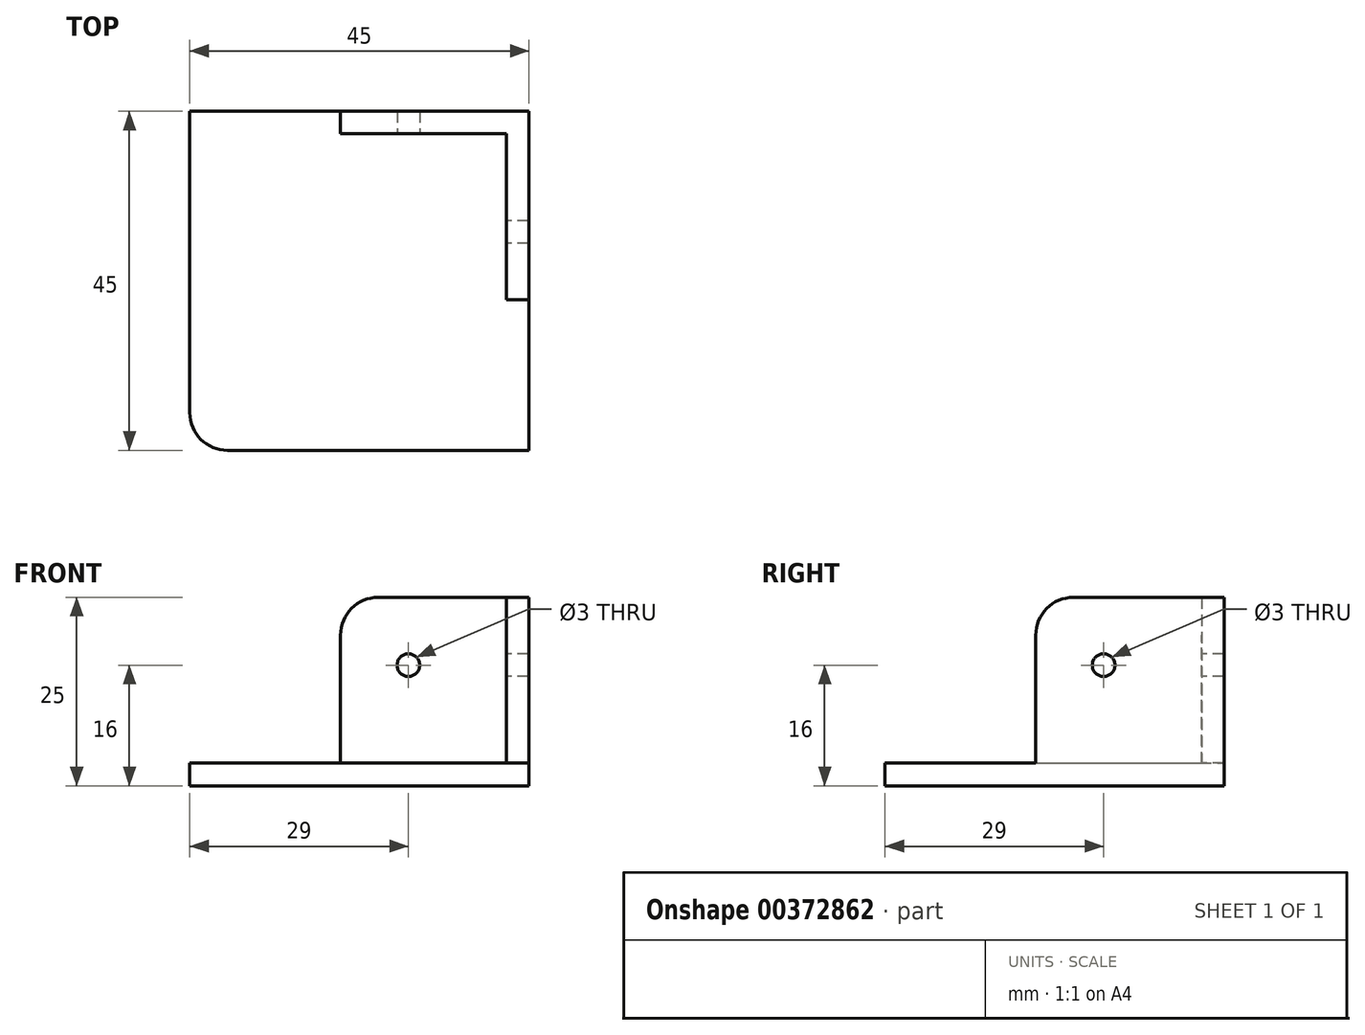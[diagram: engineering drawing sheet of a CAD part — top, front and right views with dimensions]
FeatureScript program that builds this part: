
annotation { "Feature Type Name" : "Feature", "Feature Type Description" : "" }
export const myFeature = defineFeature(function(context is Context, id is Id, definition is map)
    precondition{}
    {
        {
            var Q0;
            Q0=qCreatedBy(makeId("Top.planeOp"),FACE);
            var sketch = newSketch(context, id + "F0", { "sketchPlane" : qUnion([Q0])});
            skLineSegment(sketch, "E0.bottom", {"start": v(0, -45) * mm, "end": v(-45, -45) * mm});
            skLineSegment(sketch, "E0.top", {"start": v(0, 0) * mm, "end": v(-45, 0) * mm});
            skLineSegment(sketch, "E0.left", {"start": v(0, -45) * mm, "end": v(0, 0) * mm});
            skLineSegment(sketch, "E0.right", {"start": v(-45, -45) * mm, "end": v(-45, 0) * mm});
            skSolve(sketch);
        }
        {
            var Q0;
            Q0=qCreatedBy(makeId("Right.planeOp"),FACE);
            var sketch = newSketch(context, id + "F1", { "sketchPlane" : qUnion([Q0])});
            skLineSegment(sketch, "E1.bottom", {"start": v(-25, 0) * mm, "end": v(0, 0) * mm});
            skLineSegment(sketch, "E1.top", {"start": v(-25, 25) * mm, "end": v(0, 25) * mm});
            skLineSegment(sketch, "E1.left", {"start": v(-25, 0) * mm, "end": v(-25, 25) * mm});
            skLineSegment(sketch, "E1.right", {"start": v(0, 0) * mm, "end": v(0, 25) * mm});
            skSolve(sketch);
        }
        {
            var Q0;
            Q0=qCreatedBy(makeId("Front.planeOp"),FACE);
            var sketch = newSketch(context, id + "F2", { "sketchPlane" : qUnion([Q0])});
            skLineSegment(sketch, "E2.bottom", {"start": v(-25, 0) * mm, "end": v(0, 0) * mm});
            skLineSegment(sketch, "E2.top", {"start": v(-25, 25) * mm, "end": v(0, 25) * mm});
            skLineSegment(sketch, "E2.left", {"start": v(-25, 0) * mm, "end": v(-25, 25) * mm});
            skLineSegment(sketch, "E2.right", {"start": v(0, 0) * mm, "end": v(0, 25) * mm});
            skSolve(sketch);
        }
        {
            var Q0;
            Q0=qSketchRegion(id+"F0",true);
            extrude(context, id + "F3", {"entities" : qUnion([Q0]), "depth" : 3 * mm});
        }
        {
            var Q0;
            Q0=makeQuery(id+"F3.opExtrude","SWEPT_EDGE",EDGE,{"disambiguationData":[OSD([sQuery(id+"F0.wireOp",EDGE,"E0.bottom"),sQuery(id+"F0.wireOp",EDGE,"E0.right")])]});
            fillet(context, id + "F4", {"entities" : qUnion([Q0]), "radius" : 5 * mm, "allowEdgeOverflow" : false});
        }
        {
            var Q0;
            Q0=makeQuery(id+"F1.imprint","IMPRINT",FACE,{"disambiguationData":[TD([[makeQuery(id+"F1.imprint","IMPRINT",EDGE,{"derivedFrom":sQuery(id+"F1.wireOp",EDGE,"E1.bottom")}),1.0]])]});
            extrude(context, id + "F5", {"entities" : qUnion([Q0]), "operationType" : NewBodyOperationType.ADD, "oppositeDirection" : true, "depth" : 3 * mm});
        }
        {
            var Q0;
            Q0=makeQuery(id+"F5.opExtrude","SWEPT_EDGE",EDGE,{"disambiguationData":[OSD([sQuery(id+"F1.wireOp",EDGE,"E1.top"),sQuery(id+"F1.wireOp",EDGE,"E1.left")])]});
            fillet(context, id + "F6", {"entities" : qUnion([Q0]), "radius" : 5 * mm, "tangentPropagation" : true, "allowEdgeOverflow" : false});
        }
        {
            var Q0;
            Q0=makeQuery(id+"F2.imprint","IMPRINT",FACE,{"disambiguationData":[TD([[makeQuery(id+"F2.imprint","IMPRINT",EDGE,{"derivedFrom":sQuery(id+"F2.wireOp",EDGE,"E2.bottom")}),1.0]])]});
            extrude(context, id + "F7", {"entities" : qUnion([Q0]), "operationType" : NewBodyOperationType.ADD, "depth" : 3 * mm});
        }
        {
            var Q0;
            Q0=makeQuery(id+"F7.opExtrude","SWEPT_EDGE",EDGE,{"disambiguationData":[OSD([sQuery(id+"F2.wireOp",EDGE,"E2.top"),sQuery(id+"F2.wireOp",EDGE,"E2.left")])]});
            fillet(context, id + "F8", {"entities" : qUnion([Q0]), "radius" : 5 * mm, "tangentPropagation" : true, "allowEdgeOverflow" : false});
        }
        {
            var Q0;
            Q0=makeQuery(id+"F7.opExtrude","CAP_FACE",FACE,{"disambiguationData":[OSD([sQuery(id+"F2.wireOp",EDGE,"E2.bottom"),sQuery(id+"F2.wireOp",EDGE,"E2.top"),sQuery(id+"F2.wireOp",EDGE,"E2.left"),sQuery(id+"F2.wireOp",EDGE,"E2.right")])],"isStart":false});
            var sketch = newSketch(context, id + "F9", { "sketchPlane" : qUnion([Q0])});
            skPoint(sketch, "E3", {"position": v(-16, 16) * mm});
            skSolve(sketch);
        }
        {
            var Q0;
            Q0=sQuery(id+"F9.wireOp",VERTEX,"E3");
            var Q1;
            Q1=makeQuery(id+"F3.opExtrude","SWEPT_BODY",BODY,{"disambiguationData":[OSD([sQuery(id+"F0.wireOp",EDGE,"E0.bottom"),sQuery(id+"F0.wireOp",EDGE,"E0.top"),sQuery(id+"F0.wireOp",EDGE,"E0.left"),sQuery(id+"F0.wireOp",EDGE,"E0.right")])]});
            hole(context, id + "F10", {"style" : HoleStyle.SIMPLE, "endStyle" : HoleEndStyle.THROUGH, "holeDiameter" : 3 * mm, "isTappedThrough" : true, "tappedDepth" : 12 * mm, "tapClearance" : 3, "locations" : qUnion([Q0]), "scope" : qUnion([Q1])});
        }
        {
            var Q0;
            Q0=makeQuery(id+"F5.opExtrude","CAP_FACE",FACE,{"disambiguationData":[OSD([sQuery(id+"F1.wireOp",EDGE,"E1.bottom"),sQuery(id+"F1.wireOp",EDGE,"E1.top"),sQuery(id+"F1.wireOp",EDGE,"E1.left"),sQuery(id+"F1.wireOp",EDGE,"E1.right")])],"isStart":false});
            var sketch = newSketch(context, id + "F11", { "sketchPlane" : qUnion([Q0])});
            skPoint(sketch, "E4", {"position": v(16, 16) * mm});
            skSolve(sketch);
        }
        {
            var Q0;
            Q0=sQuery(id+"F11.wireOp",VERTEX,"E4");
            var Q1;
            Q1=makeQuery(id+"F3.opExtrude","SWEPT_BODY",BODY,{"disambiguationData":[OSD([sQuery(id+"F0.wireOp",EDGE,"E0.bottom"),sQuery(id+"F0.wireOp",EDGE,"E0.top"),sQuery(id+"F0.wireOp",EDGE,"E0.left"),sQuery(id+"F0.wireOp",EDGE,"E0.right")])]});
            hole(context, id + "F12", {"style" : HoleStyle.SIMPLE, "endStyle" : HoleEndStyle.THROUGH, "holeDiameter" : 3 * mm, "isTappedThrough" : true, "tappedDepth" : 12 * mm, "tapClearance" : 3, "locations" : qUnion([Q0]), "scope" : qUnion([Q1])});
        }
    });
